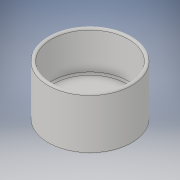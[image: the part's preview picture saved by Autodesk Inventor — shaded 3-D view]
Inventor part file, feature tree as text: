
AUTODESK INVENTOR PART (.ipt)
format: ipt  version: 2019.2 (Build 232265000, 265)  size: 266,752 bytes
history: native  units: in
note: dims shown in document units (in); Inventor stores cm internally (conversion verified against a paired STEP export)
features: extrude x3, sketch x3, fillet x1
ambient origin geometry x8: Origin, YZ Plane, XZ Plane, XY Plane, X Axis, Y Axis, Z Axis, Center Point
bodies: Solid1 (feature_tree)
feature tree (7):
  extrude  "Extrusion1"  Depth=0.25in
  extrude  "Extrusion2"  Depth=1.46in
  extrude  "Extrusion3"  Depth=0.0312in
  fillet  "Fillet2"  [1 undecoded]
  sketch  "Sketch1"  dims[d0=1.585in d1=0.25in]
  sketch  "Sketch2"  dims[d2=0.0in d3=1.46in]
  sketch  "Sketch3"  dims[d4=1.585in d5=0.75in d6=0.0in d7=0.125in d8=0.0in d10=0.0312in]
note: 1 required parameter value undecoded (feature->parameter linkage not recoverable at this tier; creation-order binding heuristic only, values carry confidence <= 0.55)
